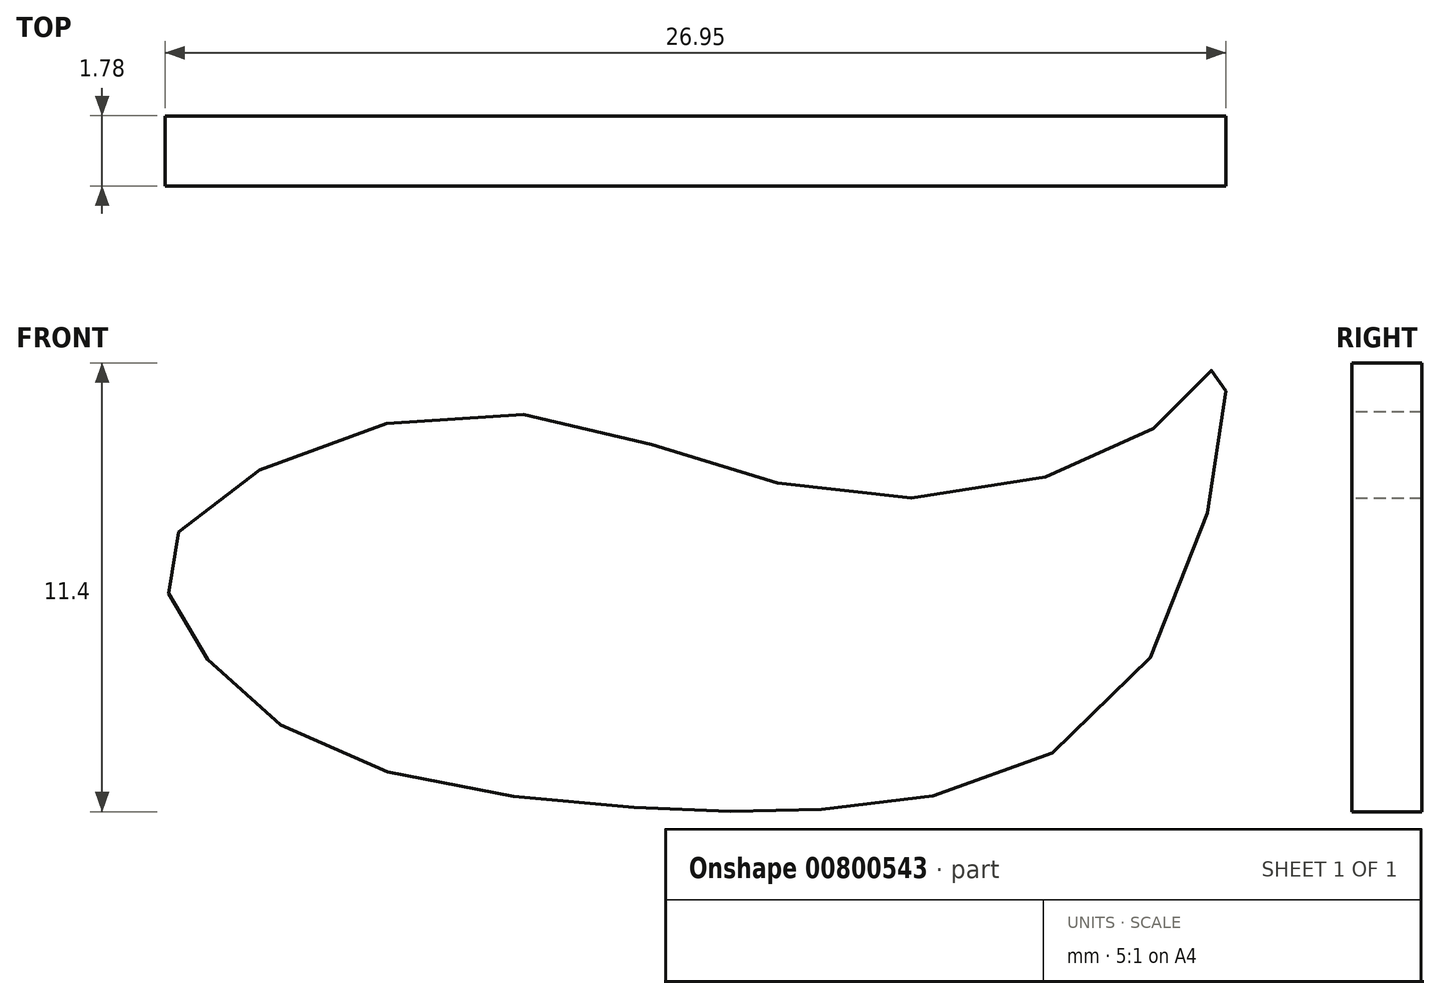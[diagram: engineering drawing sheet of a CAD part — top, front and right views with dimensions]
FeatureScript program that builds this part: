
annotation { "Feature Type Name" : "Feature", "Feature Type Description" : "" }
export const myFeature = defineFeature(function(context is Context, id is Id, definition is map)
    precondition{}
    {
        {
            var Q0;
            Q0=qCreatedBy(makeId("Front.planeOp"),FACE);
            var sketch = newSketch(context, id + "F0", { "sketchPlane" : qUnion([Q0])});
            skFitSpline(sketch, "E0", {"points": [v(-43.97, 22.78) * mm, v(-36.35, 25.83) * mm, v(-26.9, 23.7) * mm, v(-18.67, 25.83) * mm, v(-17.45, 27.05) * mm, v(-19.58, 19.13) * mm, v(-27.2, 15.77) * mm, v(-32.08, 15.77) * mm, v(-40.3, 17.3) * mm, v(-43.97, 20.65) * mm, v(-43.97, 22.78) * mm]});
            skSolve(sketch);
        }
        {
            var Q0;
            Q0=makeQuery(id+"F0.imprint","IMPRINT",FACE,{"disambiguationData":[TD([[makeQuery(id+"F0.imprint","IMPRINT",EDGE,{"derivedFrom":sQuery(id+"F0.wireOp",EDGE,"E0")}),-1.0]])]});
            extrude(context, id + "F1", {"entities" : qUnion([Q0]), "oppositeDirection" : true, "depth" : 1.78 * mm, "offsetDistance" : 25.4 * mm});
        }
    });
